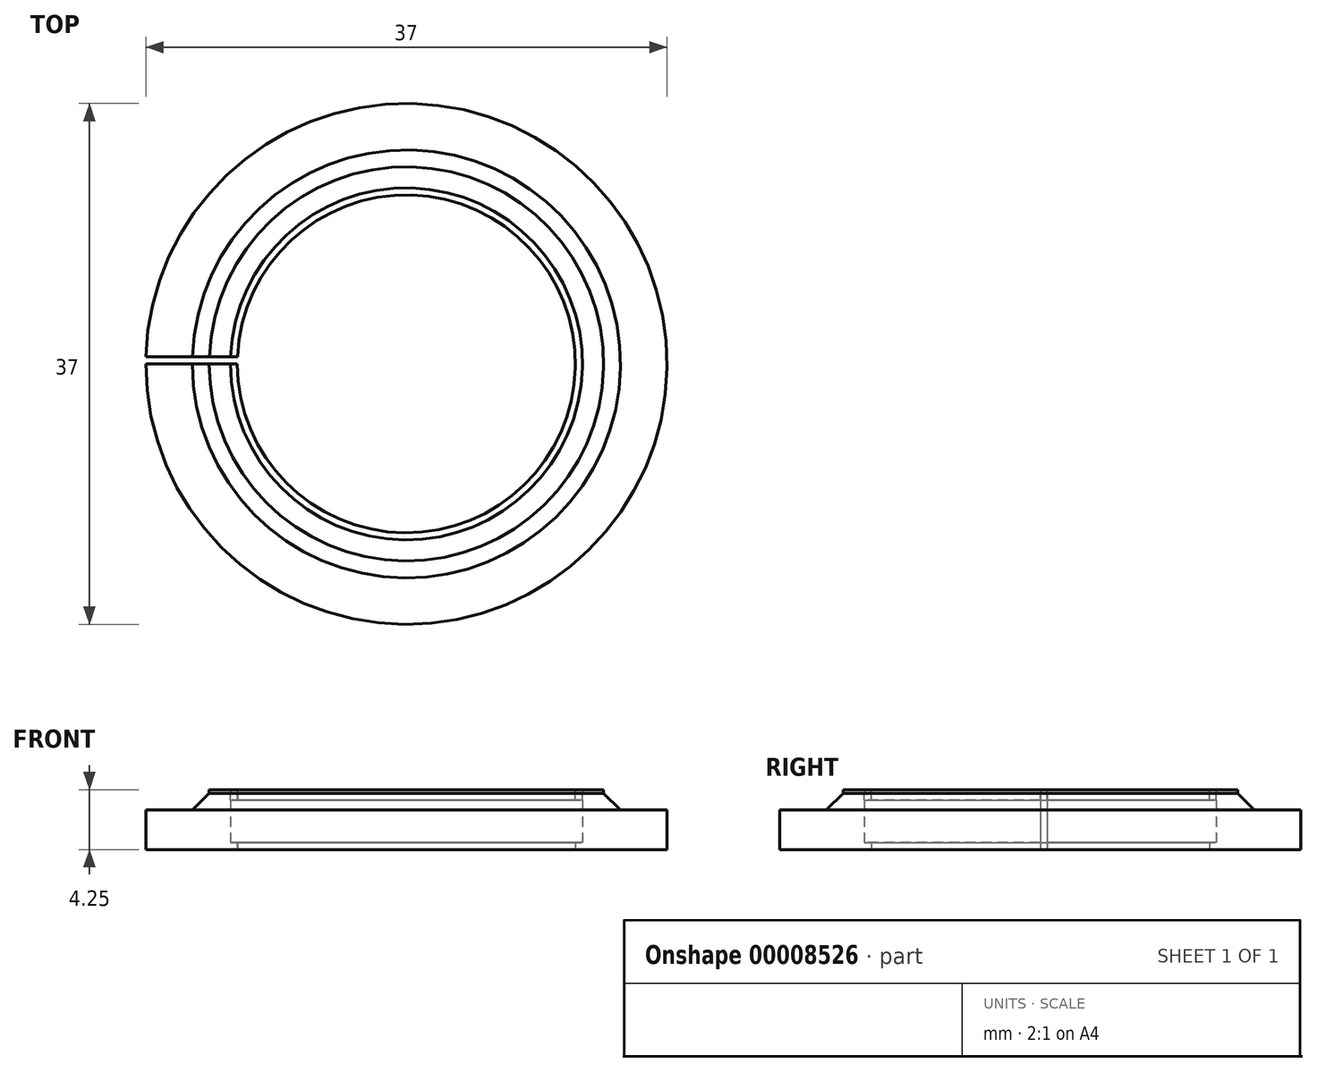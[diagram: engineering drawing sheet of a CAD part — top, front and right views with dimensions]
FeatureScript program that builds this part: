
annotation { "Feature Type Name" : "Feature", "Feature Type Description" : "" }
export const myFeature = defineFeature(function(context is Context, id is Id, definition is map)
    precondition{}
    {
        {
            var Q0;
            Q0=qCreatedBy(makeId("Top.planeOp"),FACE);
            var sketch = newSketch(context, id + "F0", { "sketchPlane" : qUnion([Q0])});
            skCircle(sketch, "E0", {"center": v(0, 0) * mm, "radius": 18.5 * mm});
            skCircle(sketch, "E1", {"center": v(0, 0) * mm, "radius": 16 * mm});
            skCircle(sketch, "E2", {"center": v(0, 0) * mm, "radius": 12.5 * mm});
            skCircle(sketch, "E3", {"center": v(0, 0) * mm, "radius": 12 * mm});
            skLineSegment(sketch, "E4", {"start": v(0, 0) * mm, "end": v(-19.51, 0) * mm});
            skLineSegment(sketch, "E5.0", {"start": v(0, 0.5) * mm, "end": v(-19.51, 0.5) * mm});
            skSolve(sketch);
        }
        {
            var Q0;
            Q0=makeQuery(id+"F0.imprint","IMPRINT",FACE,{"disambiguationData":[TD([[makeQuery(id+"F0.imprint","IMPRINT",EDGE,{"derivedFrom":sQuery(id+"F0.wireOp",EDGE,"E0")}),1.0]])]});
            extrude(context, id + "F1", {"entities" : qUnion([Q0]), "depth" : 2.8 * mm});
        }
        {
            var Q0;
            Q0=makeQuery(id+"F0.imprint","IMPRINT",FACE,{"disambiguationData":[TD([[makeQuery(id+"F0.imprint","IMPRINT",EDGE,{"derivedFrom":sQuery(id+"F0.wireOp",EDGE,"E1")}),1.0]])]});
            extrude(context, id + "F2", {"entities" : qUnion([Q0]), "operationType" : NewBodyOperationType.ADD, "depth" : 4 * mm});
        }
        {
            var Q0;
            Q0=makeQuery(id+"F0.imprint","IMPRINT",FACE,{"disambiguationData":[TD([[makeQuery(id+"F0.imprint","IMPRINT",EDGE,{"derivedFrom":sQuery(id+"F0.wireOp",EDGE,"E2")}),1.0]])]});
            extrude(context, id + "F3", {"entities" : qUnion([Q0]), "operationType" : NewBodyOperationType.ADD, "depth" : .5 * mm});
        }
        {
            var Q0;
            Q0=makeQuery(id+"F2.opExtrude","CAP_FACE",FACE,{"disambiguationData":[OSD([sQuery(id+"F0.wireOp",EDGE,"E1"),sQuery(id+"F0.wireOp",EDGE,"E2")])],"isStart":false});
            var sketch = newSketch(context, id + "F4", { "sketchPlane" : qUnion([Q0])});
            skCircle(sketch, "E6.0", {"center": v(0, 0) * mm, "radius": 12 * mm});
            skCircle(sketch, "E7.0", {"center": v(0, 0) * mm, "radius": 12.5 * mm});
            skLineSegment(sketch, "E8.0", {"start": v(0, 0.5) * mm, "end": v(-19.51, 0.5) * mm});
            skLineSegment(sketch, "E9.0", {"start": v(0, 0) * mm, "end": v(-19.51, 0) * mm});
            skSolve(sketch);
        }
        {
            var Q0;
            Q0=makeQuery(id+"F4.imprint","IMPRINT",FACE,{"disambiguationData":[TD([[makeQuery(id+"F4.imprint","IMPRINT",EDGE,{"derivedFrom":sQuery(id+"F4.wireOp",EDGE,"E6.0")}),-1.0]])]});
            extrude(context, id + "F5", {"entities" : qUnion([Q0]), "oppositeDirection" : true, "depth" : .5 * mm});
        }
        {
            var Q0;
            {var subQ3=sQuery(id+"F0.wireOp",EDGE,"E0");var subQ5=sQuery(id+"F0.wireOp",EDGE,"E4");var subQ7=makeQuery(id+"F0.imprint","INTERSECT",VERTEX,{"derivedFrom":[subQ3,subQ5]});Q0=makeQuery(id+"F0.imprint","IMPRINT",FACE,{"disambiguationData":[TD([[makeQuery(id+"F0.imprint","IMPRINT",EDGE,{"disambiguationData":[TD([[subQ7,1.0]])],"derivedFrom":subQ3}),1.0]])]});}
            var Q1;
            {var subQ3=sQuery(id+"F0.wireOp",EDGE,"E1");var subQ5=sQuery(id+"F0.wireOp",EDGE,"E4");var subQ7=makeQuery(id+"F0.imprint","INTERSECT",VERTEX,{"derivedFrom":[subQ3,subQ5]});Q1=makeQuery(id+"F0.imprint","IMPRINT",FACE,{"disambiguationData":[TD([[makeQuery(id+"F0.imprint","IMPRINT",EDGE,{"disambiguationData":[TD([[subQ7,1.0]])],"derivedFrom":subQ3}),1.0]])]});}
            var Q2;
            {var subQ1=sQuery(id+"F0.wireOp",EDGE,"E2");var subQ5=sQuery(id+"F0.wireOp",EDGE,"E4");var subQ6=makeQuery(id+"F0.imprint","INTERSECT",VERTEX,{"derivedFrom":[subQ1,subQ5]});Q2=makeQuery(id+"F0.imprint","IMPRINT",FACE,{"disambiguationData":[TD([[makeQuery(id+"F0.imprint","IMPRINT",EDGE,{"disambiguationData":[TD([[subQ6,1.0]])],"derivedFrom":subQ1}),1.0]])]});}
            extrude(context, id + "F6", {"entities" : qUnion([Q0, Q1, Q2]), "operationType" : NewBodyOperationType.REMOVE, "depth" : 25 * mm});
        }
        {
            var Q0;
            {var subQ3=sQuery(id+"F4.wireOp",EDGE,"E6.0");var subQ5=sQuery(id+"F4.wireOp",EDGE,"E8.0");var subQ7=makeQuery(id+"F4.imprint","INTERSECT",VERTEX,{"derivedFrom":[subQ3,subQ5]});Q0=makeQuery(id+"F4.imprint","IMPRINT",FACE,{"disambiguationData":[TD([[makeQuery(id+"F4.imprint","IMPRINT",EDGE,{"disambiguationData":[TD([[subQ7,-1.0]])],"derivedFrom":subQ3}),-1.0]])]});}
            extrude(context, id + "F7", {"entities" : qUnion([Q0]), "operationType" : NewBodyOperationType.REMOVE, "oppositeDirection" : true, "depth" : 25 * mm});
        }
        {
            var Q0;
            Q0=makeQuery(id+"F2.opExtrude","CAP_EDGE",EDGE,{"disambiguationData":[OSD([sQuery(id+"F0.wireOp",EDGE,"E1")])],"isStart":false});
            chamfer(context, id + "F8", {"entities" : qUnion([Q0]), "width" : 2 * mm, "tangentPropagation" : true});
        }
        {
            var Q0;
            Q0=makeQuery(id+"F2.opExtrude","CAP_FACE",FACE,{"disambiguationData":[OSD([sQuery(id+"F0.wireOp",EDGE,"E1"),sQuery(id+"F0.wireOp",EDGE,"E2")])],"isStart":false});
            var Q1;
            Q1=makeQuery(id+"F5.opExtrude","CAP_FACE",FACE,{"disambiguationData":[OSD([sQuery(id+"F4.wireOp",EDGE,"E6.0"),sQuery(id+"F4.wireOp",EDGE,"E7.0")])],"isStart":true});
            extrude(context, id + "F9", {"entities" : qUnion([Q0, Q1]), "depth" : .25 * mm});
        }
    });
